# Revit family: kitchen_Sinks_Sanindusa_Reno_Bowl-Kitchen-Sink-With-Drainer-and-Popup-Waste
name_source: partatom
category: Plumbing Fixtures
revit_build: Autodesk Revit 2018 (Build: 20170223_1515(x64)
units: mm (PartAtom-declared; Revit-internal decimal feet)

## family parameters
Cut with Voids When Loaded = No
Host = Face
Part Type = Normal
Room Calculation Point = No
Round Connector Dimension = Use Diameter
Shared = No

## types (1)
- kitchen_Sinks_Sanindusa_Reno_Bowl-Kitchen-Sink-With-Drainer-and-Popup-Waste
    AssetType = Fixed
    CodePerformance = EN 13310:2016
    Color = white
    Constituents = "Pop up waste D90 ref. 470311 (included); 
Siphon ref. 470300 (not included)"
    Default Elevation = 1219 mm
    Description = Reno 1 and 1|2 bowl kitchen sink with drainer and pop up waste
    DrainSize = 90 mm  [stored 0.295276 ft]
    Features = "Glazed on all visible sides, rectified. Double drain waste for kitchen sink, diameter 114mm
Without overflow (the water flow is ensured by the absence of a seal in one of the
covers, in case of poorly closed taps)"
    Finish = gloss
    Installation Instructions = https://www.tec.sanindusa.pt
    Manufacturer = Sanindusa
    ManufacturerName = Sanindusa
    ManufacturerURL = www.tec.sanindusa.pt
    Material = Fine Fireclay
    Model = 731100V
    ModelNumber = 731100V
    ModelReference = Reno
    Name = Reno 1 and 1|2 bowl kitchen sink
    NominalHeight = 210 mm  [stored 0.688976 ft]
    NominalLength = 1000 mm  [stored 3.28084 ft]
    NominalWidth = 500 mm  [stored 1.64042 ft]
    ProductInformation = https://www.tec.sanindusa.pt
    ProductionYear = 2020
    Shape = rectangular
    Size = 1000x500x210
    URL = www.tec.sanindusa.pt
    WarrantyDescription = https://www.tec.sanindusa.pt
    WarrantyDurationParts = 5
    WarrantyDurationUnit = year
    Waste Connection = No
    Weight = 33.00 kg

note: [stored X ft] marks values corroborated as IEEE doubles in the binary element streams (Revit-internal decimal feet)

## geometry (parser evidence)
native form markers: Sweep x4
no freeform markers — native parametric forms only
